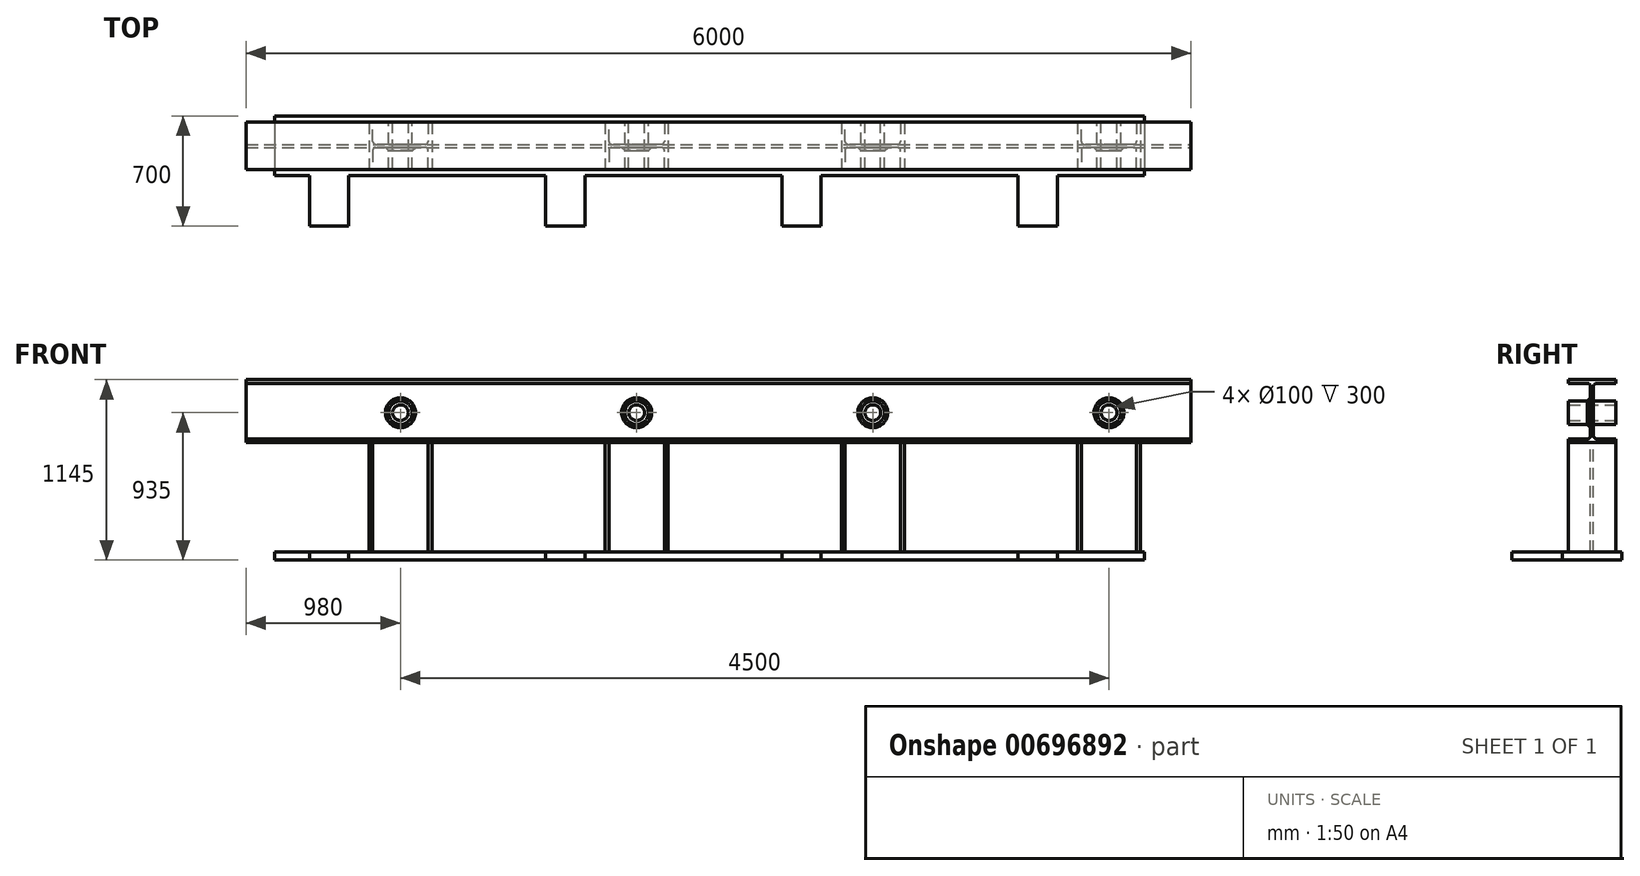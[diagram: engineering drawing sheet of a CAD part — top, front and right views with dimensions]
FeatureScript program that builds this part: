
annotation { "Feature Type Name" : "Feature", "Feature Type Description" : "" }
export const myFeature = defineFeature(function(context is Context, id is Id, definition is map)
    precondition{}
    {
        {
            var Q0;
            Q0=qCreatedBy(makeId("Right.planeOp"),FACE);
            var sketch = newSketch(context, id + "F0", { "sketchPlane" : qUnion([Q0])});
            skLineSegment(sketch, "E0", {"start": v(0, 400) * mm, "end": v(0, 0) * mm, "construction": true});
            skLineSegment(sketch, "E1", {"start": v(0, 0) * mm, "end": v(150, 0) * mm});
            skLineSegment(sketch, "E2", {"start": v(150, 0) * mm, "end": v(150, 24) * mm});
            skLineSegment(sketch, "E3", {"start": v(150, 24) * mm, "end": v(28.5, 24) * mm});
            skLineSegment(sketch, "E4", {"start": v(9.5, 43) * mm, "end": v(9.5, 357) * mm});
            skLineSegment(sketch, "E5", {"start": v(28.5, 376) * mm, "end": v(150, 376) * mm});
            skLineSegment(sketch, "E6", {"start": v(150, 376) * mm, "end": v(150, 400) * mm});
            skLineSegment(sketch, "E7", {"start": v(150, 400) * mm, "end": v(0, 400) * mm});
            skLineSegment(sketch, "E8.MirrorCS", {"start": v(-150, 0) * mm, "end": v(-150, 24) * mm});
            skLineSegment(sketch, "E9.MirrorCS", {"start": v(-150, 376) * mm, "end": v(-150, 400) * mm});
            skLineSegment(sketch, "E10.MirrorCS", {"start": v(-9.5, 43) * mm, "end": v(-9.5, 357) * mm});
            skLineSegment(sketch, "E11.MirrorCS", {"start": v(-150, 24) * mm, "end": v(-28.5, 24) * mm});
            skLineSegment(sketch, "E12.MirrorCS", {"start": v(-150, 400) * mm, "end": v(0, 400) * mm});
            skLineSegment(sketch, "E13.MirrorCS", {"start": v(0, 0) * mm, "end": v(-150, 0) * mm});
            skLineSegment(sketch, "E14.MirrorCS", {"start": v(-28.5, 376) * mm, "end": v(-150, 376) * mm});
            skPoint(sketch, "E15.visualSharp", {"position": v(9.5, 24) * mm});
            skArc(sketch, "E15.filletArc", {"start": v(9.5, 43) * mm, "mid": v(15.06, 29.56) * mm, "end": v(28.5, 24) * mm});
            skPoint(sketch, "E16.visualSharp", {"position": v(9.5, 376) * mm});
            skArc(sketch, "E16.filletArc", {"start": v(28.5, 376) * mm, "mid": v(15.06, 370.44) * mm, "end": v(9.5, 357) * mm});
            skPoint(sketch, "E17.visualSharp", {"position": v(-9.5, 376) * mm});
            skArc(sketch, "E17.filletArc", {"start": v(-9.5, 357) * mm, "mid": v(-15.06, 370.44) * mm, "end": v(-28.5, 376) * mm});
            skPoint(sketch, "E18.visualSharp", {"position": v(-9.5, 24) * mm});
            skArc(sketch, "E18.filletArc", {"start": v(-28.5, 24) * mm, "mid": v(-15.06, 29.56) * mm, "end": v(-9.5, 43) * mm});
            skSolve(sketch);
        }
        {
            var Q0;
            Q0=qSketchRegion(id+"F0",true);
            extrude(context, id + "F1", {"entities" : qUnion([Q0]), "oppositeDirection" : true, "depth" : 6000 * mm, "offsetDistance" : 25 * mm});
        }
        {
            var Q0;
            Q0=qCreatedBy(makeId("Front.planeOp"),FACE);
            var sketch = newSketch(context, id + "F2", { "sketchPlane" : qUnion([Q0])});
            skCircle(sketch, "E19", {"center": v(-520, 190) * mm, "radius": 75 * mm});
            skCircle(sketch, "E20", {"center": v(-520, 190) * mm, "radius": 50 * mm});
            skCircle(sketch, "E21.1.0.0", {"center": v(-2020, 190) * mm, "radius": 75 * mm});
            skCircle(sketch, "E21.1.0.1", {"center": v(-2020, 190) * mm, "radius": 50 * mm});
            skCircle(sketch, "E21.2.0.0", {"center": v(-3520, 190) * mm, "radius": 75 * mm});
            skCircle(sketch, "E21.2.0.1", {"center": v(-3520, 190) * mm, "radius": 50 * mm});
            skCircle(sketch, "E21.3.0.0", {"center": v(-5020, 190) * mm, "radius": 75 * mm});
            skCircle(sketch, "E21.3.0.1", {"center": v(-5020, 190) * mm, "radius": 50 * mm});
            skLineSegment(sketch, "E21.direction1", {"start": v(-520, 190) * mm, "end": v(-2020, 190) * mm, "construction": true});
            skSolve(sketch);
        }
        {
            var Q0;
            Q0=makeQuery(id+"F2.imprint","IMPRINT",FACE,{"disambiguationData":[TD([[makeQuery(id+"F2.imprint","IMPRINT",EDGE,{"derivedFrom":sQuery(id+"F2.wireOp",EDGE,"E21.3.0.0")}),1.0]])]});
            var Q1;
            Q1=makeQuery(id+"F2.imprint","IMPRINT",FACE,{"disambiguationData":[TD([[makeQuery(id+"F2.imprint","IMPRINT",EDGE,{"derivedFrom":sQuery(id+"F2.wireOp",EDGE,"E21.3.0.1")}),1.0]])]});
            var Q2;
            Q2=makeQuery(id+"F2.imprint","IMPRINT",FACE,{"disambiguationData":[TD([[makeQuery(id+"F2.imprint","IMPRINT",EDGE,{"derivedFrom":sQuery(id+"F2.wireOp",EDGE,"E21.2.0.1")}),1.0]])]});
            var Q3;
            Q3=makeQuery(id+"F2.imprint","IMPRINT",FACE,{"disambiguationData":[TD([[makeQuery(id+"F2.imprint","IMPRINT",EDGE,{"derivedFrom":sQuery(id+"F2.wireOp",EDGE,"E21.2.0.0")}),1.0]])]});
            var Q4;
            Q4=makeQuery(id+"F2.imprint","IMPRINT",FACE,{"disambiguationData":[TD([[makeQuery(id+"F2.imprint","IMPRINT",EDGE,{"derivedFrom":sQuery(id+"F2.wireOp",EDGE,"E21.1.0.0")}),1.0]])]});
            var Q5;
            Q5=makeQuery(id+"F2.imprint","IMPRINT",FACE,{"disambiguationData":[TD([[makeQuery(id+"F2.imprint","IMPRINT",EDGE,{"derivedFrom":sQuery(id+"F2.wireOp",EDGE,"E21.1.0.1")}),1.0]])]});
            var Q6;
            Q6=makeQuery(id+"F2.imprint","IMPRINT",FACE,{"disambiguationData":[TD([[makeQuery(id+"F2.imprint","IMPRINT",EDGE,{"derivedFrom":sQuery(id+"F2.wireOp",EDGE,"E20")}),1.0]])]});
            var Q7;
            Q7=makeQuery(id+"F2.imprint","IMPRINT",FACE,{"disambiguationData":[TD([[makeQuery(id+"F2.imprint","IMPRINT",EDGE,{"derivedFrom":sQuery(id+"F2.wireOp",EDGE,"E19")}),1.0]])]});
            extrude(context, id + "F3", {"entities" : qUnion([Q0, Q1, Q2, Q3, Q4, Q5, Q6, Q7]), "operationType" : NewBodyOperationType.REMOVE, "endBound" : BoundingType.SYMMETRIC, "depth" : 50 * mm, "offsetDistance" : 25 * mm});
        }
        {
            var Q0;
            Q0=qSketchRegion(id+"F2",true);
            extrude(context, id + "F4", {"entities" : qUnion([Q0]), "operationType" : NewBodyOperationType.ADD, "endBound" : BoundingType.SYMMETRIC, "depth" : 300 * mm, "offsetDistance" : 25 * mm});
        }
        {
            var Q0;
            Q0=qCreatedBy(makeId("Top.planeOp"),FACE);
            var sketch = newSketch(context, id + "F5", { "sketchPlane" : qUnion([Q0])});
            skLineSegment(sketch, "E22", {"start": v(-720, 0) * mm, "end": v(-320, 0) * mm, "construction": true});
            skLineSegment(sketch, "E23", {"start": v(-320, 0) * mm, "end": v(-320, 150) * mm});
            skLineSegment(sketch, "E24", {"start": v(-320, 150) * mm, "end": v(-344, 150) * mm});
            skLineSegment(sketch, "E25", {"start": v(-344, 150) * mm, "end": v(-344, 28.5) * mm});
            skLineSegment(sketch, "E26", {"start": v(-363, 9.5) * mm, "end": v(-677, 9.5) * mm});
            skLineSegment(sketch, "E27", {"start": v(-696, 28.5) * mm, "end": v(-696, 150) * mm});
            skLineSegment(sketch, "E28", {"start": v(-696, 150) * mm, "end": v(-720, 150) * mm});
            skLineSegment(sketch, "E29", {"start": v(-720, 150) * mm, "end": v(-720, 0) * mm});
            skPoint(sketch, "E30.visualSharp", {"position": v(-696, 9.5) * mm});
            skArc(sketch, "E30.filletArc", {"start": v(-696, 28.5) * mm, "mid": v(-690.44, 15.06) * mm, "end": v(-677, 9.5) * mm});
            skPoint(sketch, "E31.visualSharp", {"position": v(-344, 9.5) * mm});
            skArc(sketch, "E31.filletArc", {"start": v(-363, 9.5) * mm, "mid": v(-349.56, 15.06) * mm, "end": v(-344, 28.5) * mm});
            skArc(sketch, "E32.MirrorCS", {"start": v(-696, -28.5) * mm, "mid": v(-690.44, -15.06) * mm, "end": v(-677, -9.5) * mm});
            skArc(sketch, "E33.MirrorCS", {"start": v(-363, -9.5) * mm, "mid": v(-349.56, -15.06) * mm, "end": v(-344, -28.5) * mm});
            skLineSegment(sketch, "E34.MirrorCS", {"start": v(-720, -150) * mm, "end": v(-720, 0) * mm});
            skLineSegment(sketch, "E35.MirrorCS", {"start": v(-696, -150) * mm, "end": v(-720, -150) * mm});
            skLineSegment(sketch, "E36.MirrorCS", {"start": v(-696, -28.5) * mm, "end": v(-696, -150) * mm});
            skLineSegment(sketch, "E37.MirrorCS", {"start": v(-320, -150) * mm, "end": v(-344, -150) * mm});
            skLineSegment(sketch, "E38.MirrorCS", {"start": v(-344, -150) * mm, "end": v(-344, -28.5) * mm});
            skLineSegment(sketch, "E39.MirrorCS", {"start": v(-363, -9.5) * mm, "end": v(-677, -9.5) * mm});
            skPoint(sketch, "E40.MirrorP", {"position": v(-344, -9.5) * mm});
            skPoint(sketch, "E41.MirrorP", {"position": v(-696, -9.5) * mm});
            skLineSegment(sketch, "E42.MirrorCS", {"start": v(-320, 0) * mm, "end": v(-320, -150) * mm});
            skLineSegment(sketch, "E43.1.0.0", {"start": v(-1820, 0) * mm, "end": v(-1820, -150) * mm});
            skPoint(sketch, "E43.1.0.1", {"position": v(-2196, -9.5) * mm});
            skLineSegment(sketch, "E43.1.0.2", {"start": v(-1844, -150) * mm, "end": v(-1844, -28.5) * mm});
            skLineSegment(sketch, "E43.1.0.3", {"start": v(-2196, -28.5) * mm, "end": v(-2196, -150) * mm});
            skLineSegment(sketch, "E43.1.0.4", {"start": v(-2220, 0) * mm, "end": v(-1820, 0) * mm, "construction": true});
            skLineSegment(sketch, "E43.1.0.5", {"start": v(-1820, 0) * mm, "end": v(-1820, 150) * mm});
            skLineSegment(sketch, "E43.1.0.6", {"start": v(-1844, 150) * mm, "end": v(-1844, 28.5) * mm});
            skLineSegment(sketch, "E43.1.0.7", {"start": v(-1863, 9.5) * mm, "end": v(-2177, 9.5) * mm});
            skLineSegment(sketch, "E43.1.0.8", {"start": v(-2196, 28.5) * mm, "end": v(-2196, 150) * mm});
            skLineSegment(sketch, "E43.1.0.9", {"start": v(-2220, 150) * mm, "end": v(-2220, 0) * mm});
            skLineSegment(sketch, "E43.1.0.10", {"start": v(-2220, -150) * mm, "end": v(-2220, 0) * mm});
            skPoint(sketch, "E43.1.0.11", {"position": v(-1844, -9.5) * mm});
            skLineSegment(sketch, "E43.1.0.12", {"start": v(-1863, -9.5) * mm, "end": v(-2177, -9.5) * mm});
            skPoint(sketch, "E43.1.0.13", {"position": v(-1844, 9.5) * mm});
            skPoint(sketch, "E43.1.0.14", {"position": v(-2196, 9.5) * mm});
            skLineSegment(sketch, "E43.1.0.15", {"start": v(-2196, -150) * mm, "end": v(-2220, -150) * mm});
            skLineSegment(sketch, "E43.1.0.16", {"start": v(-1820, -150) * mm, "end": v(-1844, -150) * mm});
            skLineSegment(sketch, "E43.1.0.17", {"start": v(-1820, 150) * mm, "end": v(-1844, 150) * mm});
            skLineSegment(sketch, "E43.1.0.18", {"start": v(-2196, 150) * mm, "end": v(-2220, 150) * mm});
            skArc(sketch, "E43.1.0.19", {"start": v(-2196, 28.5) * mm, "mid": v(-2190.44, 15.06) * mm, "end": v(-2177, 9.5) * mm});
            skArc(sketch, "E43.1.0.20", {"start": v(-1863, 9.5) * mm, "mid": v(-1849.56, 15.06) * mm, "end": v(-1844, 28.5) * mm});
            skArc(sketch, "E43.1.0.21", {"start": v(-2196, -28.5) * mm, "mid": v(-2190.44, -15.06) * mm, "end": v(-2177, -9.5) * mm});
            skArc(sketch, "E43.1.0.22", {"start": v(-1863, -9.5) * mm, "mid": v(-1849.56, -15.06) * mm, "end": v(-1844, -28.5) * mm});
            skLineSegment(sketch, "E43.2.0.0", {"start": v(-3320, 0) * mm, "end": v(-3320, -150) * mm});
            skPoint(sketch, "E43.2.0.1", {"position": v(-3696, -9.5) * mm});
            skLineSegment(sketch, "E43.2.0.2", {"start": v(-3344, -150) * mm, "end": v(-3344, -28.5) * mm});
            skLineSegment(sketch, "E43.2.0.3", {"start": v(-3696, -28.5) * mm, "end": v(-3696, -150) * mm});
            skLineSegment(sketch, "E43.2.0.4", {"start": v(-3720, 0) * mm, "end": v(-3320, 0) * mm, "construction": true});
            skLineSegment(sketch, "E43.2.0.5", {"start": v(-3320, 0) * mm, "end": v(-3320, 150) * mm});
            skLineSegment(sketch, "E43.2.0.6", {"start": v(-3344, 150) * mm, "end": v(-3344, 28.5) * mm});
            skLineSegment(sketch, "E43.2.0.7", {"start": v(-3363, 9.5) * mm, "end": v(-3677, 9.5) * mm});
            skLineSegment(sketch, "E43.2.0.8", {"start": v(-3696, 28.5) * mm, "end": v(-3696, 150) * mm});
            skLineSegment(sketch, "E43.2.0.9", {"start": v(-3720, 150) * mm, "end": v(-3720, 0) * mm});
            skLineSegment(sketch, "E43.2.0.10", {"start": v(-3720, -150) * mm, "end": v(-3720, 0) * mm});
            skPoint(sketch, "E43.2.0.11", {"position": v(-3344, -9.5) * mm});
            skLineSegment(sketch, "E43.2.0.12", {"start": v(-3363, -9.5) * mm, "end": v(-3677, -9.5) * mm});
            skPoint(sketch, "E43.2.0.13", {"position": v(-3344, 9.5) * mm});
            skPoint(sketch, "E43.2.0.14", {"position": v(-3696, 9.5) * mm});
            skLineSegment(sketch, "E43.2.0.15", {"start": v(-3696, -150) * mm, "end": v(-3720, -150) * mm});
            skLineSegment(sketch, "E43.2.0.16", {"start": v(-3320, -150) * mm, "end": v(-3344, -150) * mm});
            skLineSegment(sketch, "E43.2.0.17", {"start": v(-3320, 150) * mm, "end": v(-3344, 150) * mm});
            skLineSegment(sketch, "E43.2.0.18", {"start": v(-3696, 150) * mm, "end": v(-3720, 150) * mm});
            skArc(sketch, "E43.2.0.19", {"start": v(-3696, 28.5) * mm, "mid": v(-3690.44, 15.06) * mm, "end": v(-3677, 9.5) * mm});
            skArc(sketch, "E43.2.0.20", {"start": v(-3363, 9.5) * mm, "mid": v(-3349.56, 15.06) * mm, "end": v(-3344, 28.5) * mm});
            skArc(sketch, "E43.2.0.21", {"start": v(-3696, -28.5) * mm, "mid": v(-3690.44, -15.06) * mm, "end": v(-3677, -9.5) * mm});
            skArc(sketch, "E43.2.0.22", {"start": v(-3363, -9.5) * mm, "mid": v(-3349.56, -15.06) * mm, "end": v(-3344, -28.5) * mm});
            skLineSegment(sketch, "E43.direction1", {"start": v(-2220, -150) * mm, "end": v(-720, -150) * mm, "construction": true});
            skLineSegment(sketch, "E44.0.3.0", {"start": v(-4820, 0) * mm, "end": v(-4820, -150) * mm});
            skPoint(sketch, "E44.3.3.0", {"position": v(-5196, -9.5) * mm});
            skLineSegment(sketch, "E44.4.3.0", {"start": v(-4844, -150) * mm, "end": v(-4844, -28.5) * mm});
            skLineSegment(sketch, "E44.7.3.0", {"start": v(-5196, -28.5) * mm, "end": v(-5196, -150) * mm});
            skLineSegment(sketch, "E44.10.3.0", {"start": v(-5220, 0) * mm, "end": v(-4820, 0) * mm, "construction": true});
            skLineSegment(sketch, "E44.13.3.0", {"start": v(-4820, 0) * mm, "end": v(-4820, 150) * mm});
            skLineSegment(sketch, "E44.16.3.0", {"start": v(-4844, 150) * mm, "end": v(-4844, 28.5) * mm});
            skLineSegment(sketch, "E44.19.3.0", {"start": v(-4863, 9.5) * mm, "end": v(-5177, 9.5) * mm});
            skLineSegment(sketch, "E44.22.3.0", {"start": v(-5196, 28.5) * mm, "end": v(-5196, 150) * mm});
            skLineSegment(sketch, "E44.25.3.0", {"start": v(-5220, 150) * mm, "end": v(-5220, 0) * mm});
            skLineSegment(sketch, "E44.28.3.0", {"start": v(-5220, -150) * mm, "end": v(-5220, 0) * mm});
            skPoint(sketch, "E44.31.3.0", {"position": v(-4844, -9.5) * mm});
            skLineSegment(sketch, "E44.32.3.0", {"start": v(-4863, -9.5) * mm, "end": v(-5177, -9.5) * mm});
            skPoint(sketch, "E44.35.3.0", {"position": v(-4844, 9.5) * mm});
            skPoint(sketch, "E44.36.3.0", {"position": v(-5196, 9.5) * mm});
            skLineSegment(sketch, "E44.37.3.0", {"start": v(-5196, -150) * mm, "end": v(-5220, -150) * mm});
            skLineSegment(sketch, "E44.40.3.0", {"start": v(-4820, -150) * mm, "end": v(-4844, -150) * mm});
            skLineSegment(sketch, "E44.43.3.0", {"start": v(-4820, 150) * mm, "end": v(-4844, 150) * mm});
            skLineSegment(sketch, "E44.46.3.0", {"start": v(-5196, 150) * mm, "end": v(-5220, 150) * mm});
            skArc(sketch, "E44.49.3.0", {"start": v(-5196, 28.5) * mm, "mid": v(-5190.44, 15.06) * mm, "end": v(-5177, 9.5) * mm});
            skArc(sketch, "E44.53.3.0", {"start": v(-4863, 9.5) * mm, "mid": v(-4849.56, 15.06) * mm, "end": v(-4844, 28.5) * mm});
            skArc(sketch, "E44.57.3.0", {"start": v(-5196, -28.5) * mm, "mid": v(-5190.44, -15.06) * mm, "end": v(-5177, -9.5) * mm});
            skArc(sketch, "E44.61.3.0", {"start": v(-4863, -9.5) * mm, "mid": v(-4849.56, -15.06) * mm, "end": v(-4844, -28.5) * mm});
            skSolve(sketch);
        }
        {
            var Q0;
            Q0=makeQuery(id+"F5.imprint","IMPRINT",FACE,{"disambiguationData":[TD([[makeQuery(id+"F5.imprint","IMPRINT",EDGE,{"derivedFrom":sQuery(id+"F5.wireOp",EDGE,"E23")}),1.0]])]});
            var Q1;
            Q1=makeQuery(id+"F5.imprint","IMPRINT",FACE,{"disambiguationData":[TD([[makeQuery(id+"F5.imprint","IMPRINT",EDGE,{"derivedFrom":sQuery(id+"F5.wireOp",EDGE,"E43.1.0.0")}),-1.0]])]});
            var Q2;
            Q2=makeQuery(id+"F5.imprint","IMPRINT",FACE,{"disambiguationData":[TD([[makeQuery(id+"F5.imprint","IMPRINT",EDGE,{"derivedFrom":sQuery(id+"F5.wireOp",EDGE,"E43.2.0.0")}),-1.0]])]});
            var Q3;
            Q3=makeQuery(id+"F5.imprint","IMPRINT",FACE,{"disambiguationData":[TD([[makeQuery(id+"F5.imprint","IMPRINT",EDGE,{"derivedFrom":sQuery(id+"F5.wireOp",EDGE,"E44.0.3.0")}),-1.0]])]});
            extrude(context, id + "F6", {"entities" : qUnion([Q0, Q1, Q2, Q3]), "depth" : -695 * mm, "offsetDistance" : 25 * mm});
        }
        {
            var Q0;
            Q0=makeQuery(id+"F6.opExtrude","CAP_FACE",FACE,{"disambiguationData":[OSD([sQuery(id+"F5.wireOp",EDGE,"E43.2.0.0"),sQuery(id+"F5.wireOp",EDGE,"E43.2.0.2"),sQuery(id+"F5.wireOp",EDGE,"E43.2.0.3"),sQuery(id+"F5.wireOp",EDGE,"E43.2.0.5"),sQuery(id+"F5.wireOp",EDGE,"E43.2.0.6"),sQuery(id+"F5.wireOp",EDGE,"E43.2.0.7"),sQuery(id+"F5.wireOp",EDGE,"E43.2.0.8"),sQuery(id+"F5.wireOp",EDGE,"E43.2.0.9"),sQuery(id+"F5.wireOp",EDGE,"E43.2.0.10"),sQuery(id+"F5.wireOp",EDGE,"E43.2.0.12"),sQuery(id+"F5.wireOp",EDGE,"E43.2.0.15"),sQuery(id+"F5.wireOp",EDGE,"E43.2.0.16"),sQuery(id+"F5.wireOp",EDGE,"E43.2.0.17"),sQuery(id+"F5.wireOp",EDGE,"E43.2.0.18"),sQuery(id+"F5.wireOp",EDGE,"E43.2.0.19"),sQuery(id+"F5.wireOp",EDGE,"E43.2.0.20"),sQuery(id+"F5.wireOp",EDGE,"E43.2.0.21"),sQuery(id+"F5.wireOp",EDGE,"E43.2.0.22")])],"isStart":false});
            var sketch = newSketch(context, id + "F7", { "sketchPlane" : qUnion([Q0])});
            skLineSegment(sketch, "E45.bottom", {"start": v(-5820, -190) * mm, "end": v(-295, -190) * mm});
            skLineSegment(sketch, "E45.top", {"start": v(-5820, 190) * mm, "end": v(-295, 190) * mm});
            skLineSegment(sketch, "E45.left", {"start": v(-5820, -190) * mm, "end": v(-5820, 190) * mm});
            skLineSegment(sketch, "E45.right", {"start": v(-295, -190) * mm, "end": v(-295, 190) * mm});
            skSolve(sketch);
        }
        {
            var Q0;
            Q0=qSketchRegion(id+"F7",true);
            extrude(context, id + "F8", {"entities" : qUnion([Q0]), "depth" : 50 * mm, "offsetDistance" : 25 * mm});
        }
        {
            var Q0;
            Q0=makeQuery(id+"F3.boolean.opBoolean","INTERSECT",EDGE,{"derivedFrom":[makeQuery(id+"F1.opExtrude","SWEPT_FACE",FACE,{"disambiguationData":[OSD([sQuery(id+"F0.wireOp",EDGE,"E10.MirrorCS")])]}),makeQuery(id+"F3.opExtrude","SWEPT_FACE",FACE,{"disambiguationData":[OSD([sQuery(id+"F2.wireOp",EDGE,"E21.3.0.0")])]})]});
            var Q1;
            Q1=makeQuery(id+"F3.boolean.opBoolean","INTERSECT",EDGE,{"derivedFrom":[makeQuery(id+"F1.opExtrude","SWEPT_FACE",FACE,{"disambiguationData":[OSD([sQuery(id+"F0.wireOp",EDGE,"E10.MirrorCS")])]}),makeQuery(id+"F3.opExtrude","SWEPT_FACE",FACE,{"disambiguationData":[OSD([sQuery(id+"F2.wireOp",EDGE,"E21.2.0.0")])]})]});
            var Q2;
            Q2=makeQuery(id+"F3.boolean.opBoolean","INTERSECT",EDGE,{"derivedFrom":[makeQuery(id+"F1.opExtrude","SWEPT_FACE",FACE,{"disambiguationData":[OSD([sQuery(id+"F0.wireOp",EDGE,"E10.MirrorCS")])]}),makeQuery(id+"F3.opExtrude","SWEPT_FACE",FACE,{"disambiguationData":[OSD([sQuery(id+"F2.wireOp",EDGE,"E21.1.0.0")])]})]});
            var Q3;
            Q3=makeQuery(id+"F3.boolean.opBoolean","INTERSECT",EDGE,{"derivedFrom":[makeQuery(id+"F1.opExtrude","SWEPT_FACE",FACE,{"disambiguationData":[OSD([sQuery(id+"F0.wireOp",EDGE,"E10.MirrorCS")])]}),makeQuery(id+"F3.opExtrude","SWEPT_FACE",FACE,{"disambiguationData":[OSD([sQuery(id+"F2.wireOp",EDGE,"E19")])]})]});
            var Q4;
            Q4=makeQuery(id+"F3.boolean.opBoolean","INTERSECT",EDGE,{"derivedFrom":[makeQuery(id+"F1.opExtrude","SWEPT_FACE",FACE,{"disambiguationData":[OSD([sQuery(id+"F0.wireOp",EDGE,"E4")])]}),makeQuery(id+"F3.opExtrude","SWEPT_FACE",FACE,{"disambiguationData":[OSD([sQuery(id+"F2.wireOp",EDGE,"E19")])]})]});
            var Q5;
            Q5=makeQuery(id+"F3.boolean.opBoolean","INTERSECT",EDGE,{"derivedFrom":[makeQuery(id+"F1.opExtrude","SWEPT_FACE",FACE,{"disambiguationData":[OSD([sQuery(id+"F0.wireOp",EDGE,"E4")])]}),makeQuery(id+"F3.opExtrude","SWEPT_FACE",FACE,{"disambiguationData":[OSD([sQuery(id+"F2.wireOp",EDGE,"E21.1.0.0")])]})]});
            var Q6;
            Q6=makeQuery(id+"F3.boolean.opBoolean","INTERSECT",EDGE,{"derivedFrom":[makeQuery(id+"F1.opExtrude","SWEPT_FACE",FACE,{"disambiguationData":[OSD([sQuery(id+"F0.wireOp",EDGE,"E4")])]}),makeQuery(id+"F3.opExtrude","SWEPT_FACE",FACE,{"disambiguationData":[OSD([sQuery(id+"F2.wireOp",EDGE,"E21.2.0.0")])]})]});
            var Q7;
            Q7=makeQuery(id+"F3.boolean.opBoolean","INTERSECT",EDGE,{"derivedFrom":[makeQuery(id+"F1.opExtrude","SWEPT_FACE",FACE,{"disambiguationData":[OSD([sQuery(id+"F0.wireOp",EDGE,"E4")])]}),makeQuery(id+"F3.opExtrude","SWEPT_FACE",FACE,{"disambiguationData":[OSD([sQuery(id+"F2.wireOp",EDGE,"E21.3.0.0")])]})]});
            chamfer(context, id + "F9", {"entities" : qUnion([Q0, Q1, Q2, Q3, Q4, Q5, Q6, Q7]), "width" : 20 * mm, "tangentPropagation" : true});
        }
        {
            var Q0;
            Q0=makeQuery(id+"F8.opExtrude","CAP_FACE",FACE,{"disambiguationData":[OSD([sQuery(id+"F7.wireOp",EDGE,"E45.bottom"),sQuery(id+"F7.wireOp",EDGE,"E45.top"),sQuery(id+"F7.wireOp",EDGE,"E45.left"),sQuery(id+"F7.wireOp",EDGE,"E45.right")])],"isStart":false});
            var sketch = newSketch(context, id + "F10", { "sketchPlane" : qUnion([Q0])});
            skLineSegment(sketch, "E46.bottom", {"start": v(-1098, 190) * mm, "end": v(-848, 190) * mm});
            skLineSegment(sketch, "E46.top", {"start": v(-1098, 510) * mm, "end": v(-848, 510) * mm});
            skLineSegment(sketch, "E46.left", {"start": v(-1098, 190) * mm, "end": v(-1098, 510) * mm});
            skLineSegment(sketch, "E46.right", {"start": v(-848, 190) * mm, "end": v(-848, 510) * mm});
            skLineSegment(sketch, "E47.1.0.0", {"start": v(-2598, 190) * mm, "end": v(-2348, 190) * mm});
            skLineSegment(sketch, "E47.1.0.1", {"start": v(-2598, 510) * mm, "end": v(-2348, 510) * mm});
            skLineSegment(sketch, "E47.1.0.2", {"start": v(-2598, 190) * mm, "end": v(-2598, 510) * mm});
            skLineSegment(sketch, "E47.1.0.3", {"start": v(-2348, 190) * mm, "end": v(-2348, 510) * mm});
            skLineSegment(sketch, "E47.2.0.0", {"start": v(-4098, 190) * mm, "end": v(-3848, 190) * mm});
            skLineSegment(sketch, "E47.2.0.1", {"start": v(-4098, 510) * mm, "end": v(-3848, 510) * mm});
            skLineSegment(sketch, "E47.2.0.2", {"start": v(-4098, 190) * mm, "end": v(-4098, 510) * mm});
            skLineSegment(sketch, "E47.2.0.3", {"start": v(-3848, 190) * mm, "end": v(-3848, 510) * mm});
            skLineSegment(sketch, "E47.3.0.0", {"start": v(-5598, 190) * mm, "end": v(-5348, 190) * mm});
            skLineSegment(sketch, "E47.3.0.1", {"start": v(-5598, 510) * mm, "end": v(-5348, 510) * mm});
            skLineSegment(sketch, "E47.3.0.2", {"start": v(-5598, 190) * mm, "end": v(-5598, 510) * mm});
            skLineSegment(sketch, "E47.3.0.3", {"start": v(-5348, 190) * mm, "end": v(-5348, 510) * mm});
            skLineSegment(sketch, "E47.direction1", {"start": v(-1098, 190) * mm, "end": v(-2598, 190) * mm, "construction": true});
            skSolve(sketch);
        }
        {
            var Q0;
            Q0 = qSketchRegion(id + "F10", true);
            extrude(context, id + "F11", {"entities" : qUnion([Q0]), "operationType" : NewBodyOperationType.ADD, "oppositeDirection" : true, "depth" : 50 * mm, "offsetDistance" : 25 * mm});
        }
    });
